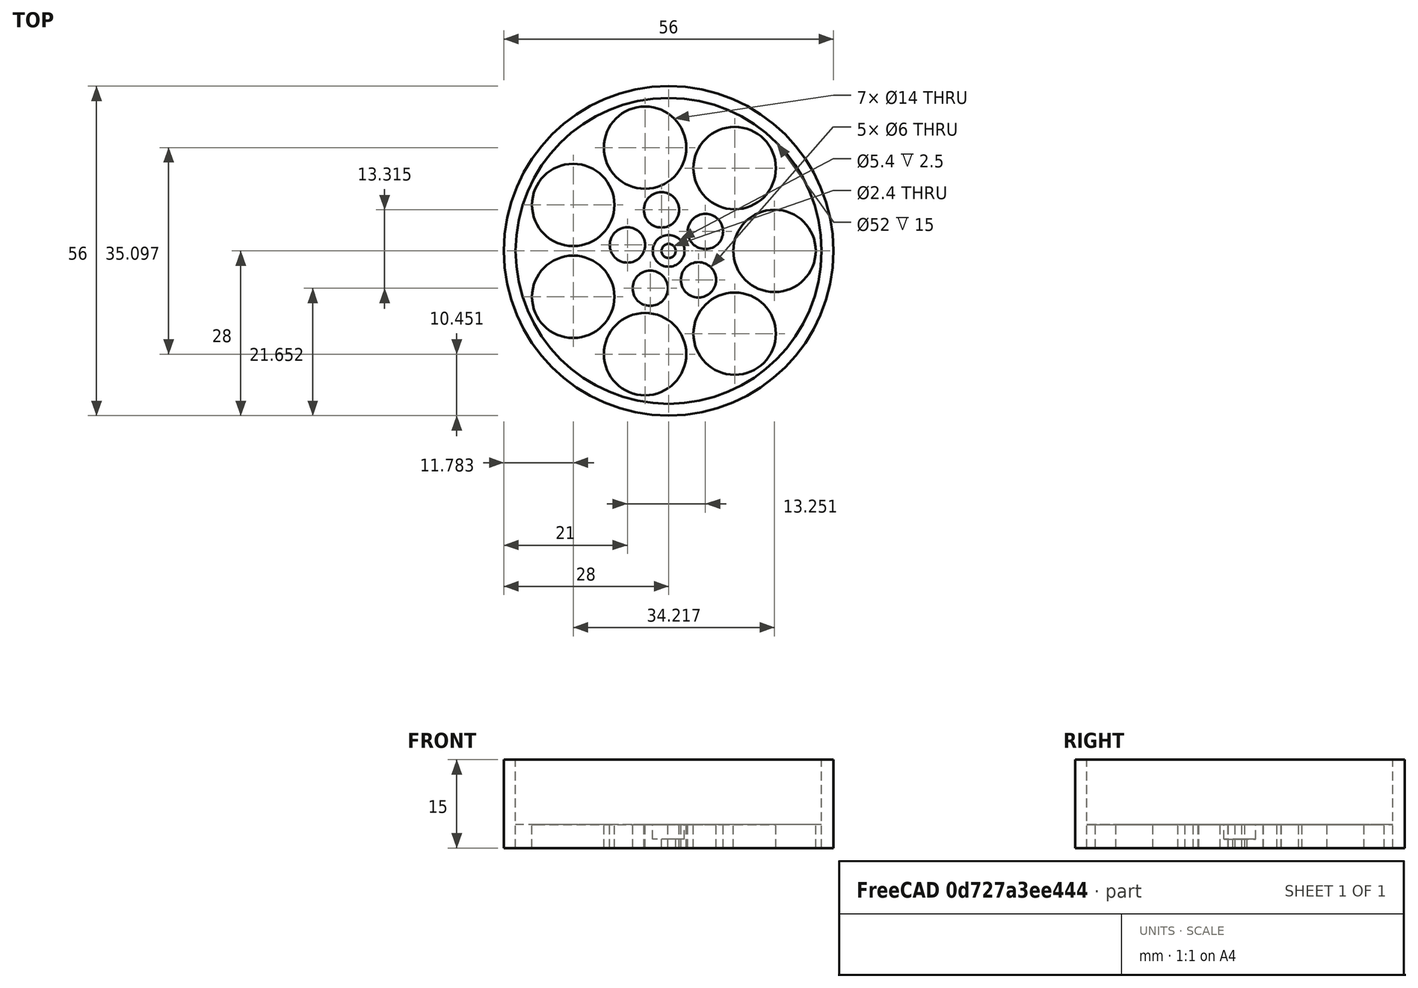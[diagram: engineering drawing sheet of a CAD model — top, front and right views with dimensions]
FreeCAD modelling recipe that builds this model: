
FCSTD DOCUMENT  (FreeCAD 0.16R6712 (Git))
Label: roda_forats
License: All rights reserved
LicenseURL: http://en.wikipedia.org/wiki/All_rights_reserved
objects: Part::Cylinder×7, Part::Cut×5, Part::FeaturePython×2
note: 14 computed .brp shape members not serialized (recipe doc carries the construction recipe); baked Part::Feature solids carry a one-line shape summary decoded from their .brp

FEATURE [Part::Cylinder] Cylinder  label="gross"
  Angle = 360
  Height = 4
  Placement = pos=(0,0,-1) rot=(0,0,1;0rad)
  Radius = 26
FEATURE [Part::Cylinder] Cylinder001  label="interior"
  Angle = 360
  Height = 6
  Placement = pos=(0,0,0.5) rot=(0,0,1;0rad)
  Radius = 2.7
FEATURE [Part::Cylinder] Cylinder002  label="Cylinder"
  Angle = 360
  Height = 7
  Placement = pos=(0,0,-1) rot=(0,0,1;0rad)
  Radius = 1.2
FEATURE [Part::Cut] Cut
  Base = -> Cylinder
  Tool = -> Cylinder002
FEATURE [Part::Cut] Cut001
  Base = -> Cut
  Placement = pos=(0,0,1) rot=(0,0,1;0rad)
  Tool = -> Cylinder001
FEATURE [Part::Cylinder] Cylinder004  label="fora_gran"
  Angle = 360
  Height = 15
  Placement = pos=(0,0,1) rot=(0,0,1;0rad)
  Radius = 28
FEATURE [Part::Cylinder] Cylinder005  label="forat_gran"
  Angle = 360
  Height = 15
  Placement = pos=(0,0,1) rot=(0,0,1;0rad)
  Radius = 26
FEATURE [Part::Cut] Cut002
  Base = -> Cylinder004
  Placement = pos=(0,0,-1) rot=(0,0,1;0rad)
  Tool = -> Cylinder005
FEATURE [Part::Cylinder] Cylinder006  label="forat roda"
  Angle = 360
  Height = 10
  Placement = pos=(18,0,-2) rot=(0,0,1;0rad)
  Radius = 7
FEATURE [Part::FeaturePython] Array  label="array forat"  # Draft array (typed FeaturePython)
  Angle = 360
  ArrayType = 1
  Axis = (0,0,1)
  Base = -> Cylinder006
  Center = (0,0,0)
  Fuse = false
  IntervalAxis = (0,0,0)
  IntervalX = (1,0,0)
  IntervalY = (0,1,0)
  IntervalZ = (0,0,0)
  NumberPolar = 7
  NumberX = 2
  NumberY = 2
  NumberZ = 1
FEATURE [Part::Cut] Cut003
  Base = -> Cut001
  Tool = -> Array
FEATURE [Part::Cylinder] Cylinder007  label="forat_petit"
  Angle = 360
  Height = 10
  Placement = pos=(-7,1,-2) rot=(0,0,1;0rad)
  Radius = 3
FEATURE [Part::FeaturePython] Array001  # Draft array (typed FeaturePython)
  Angle = 360
  ArrayType = 1
  Axis = (0,0,1)
  Base = -> Cylinder007
  Center = (0,0,0)
  Fuse = false
  IntervalAxis = (0,0,0)
  IntervalX = (1,0,0)
  IntervalY = (0,1,0)
  IntervalZ = (0,0,0)
  NumberPolar = 5
  NumberX = 2
  NumberY = 2
  NumberZ = 1
FEATURE [Part::Cut] Cut004
  Base = -> Cut003
  Tool = -> Array001
